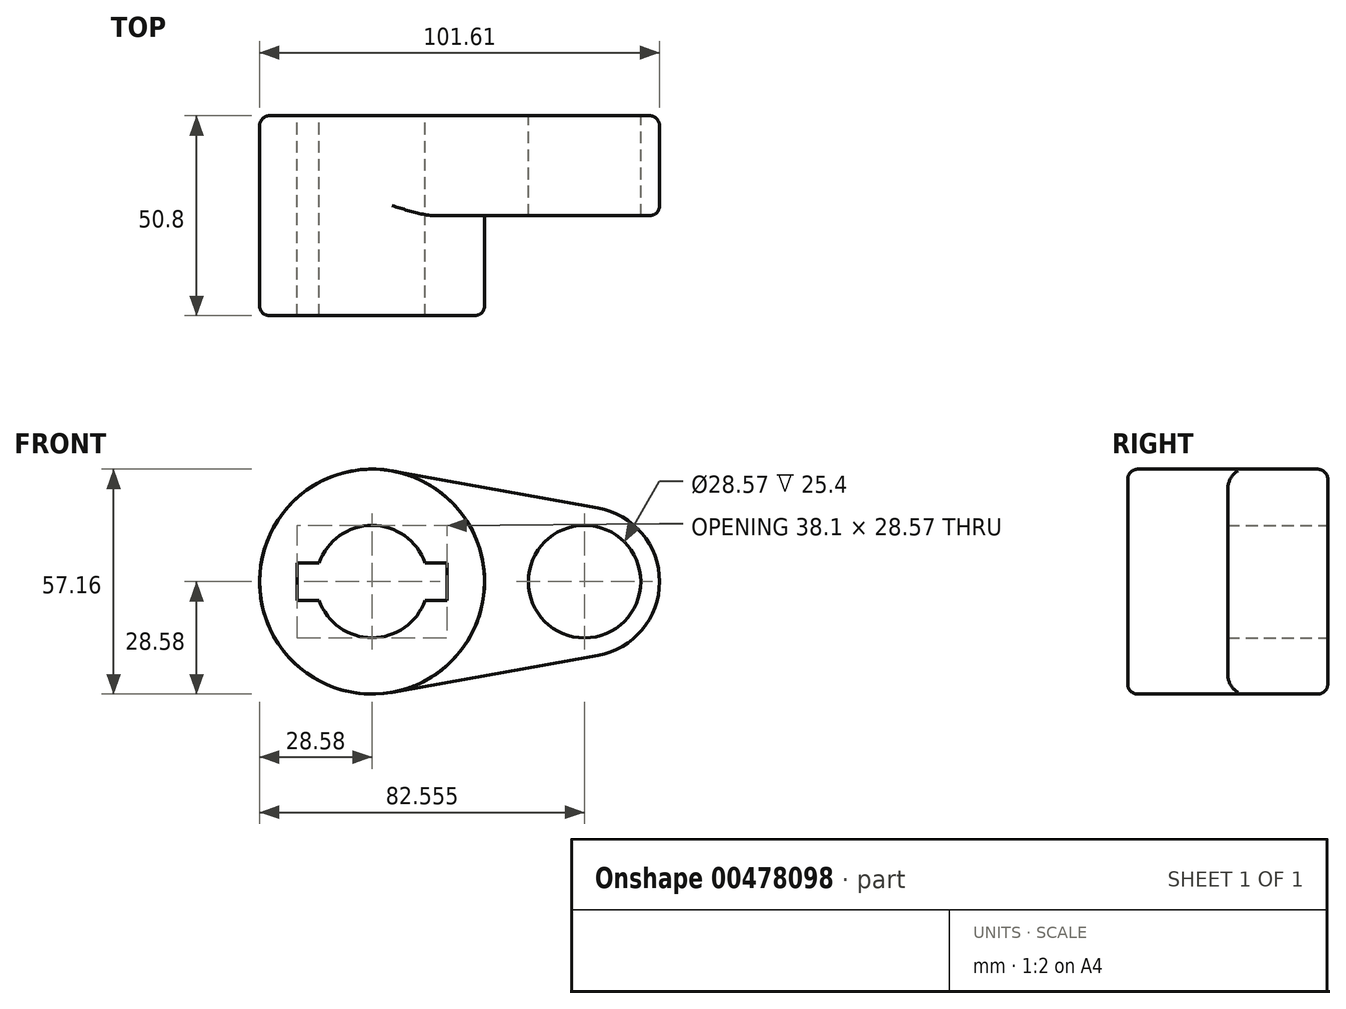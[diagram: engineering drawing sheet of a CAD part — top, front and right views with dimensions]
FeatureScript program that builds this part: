
annotation { "Feature Type Name" : "Feature", "Feature Type Description" : "" }
export const myFeature = defineFeature(function(context is Context, id is Id, definition is map)
    precondition{}
    {
        {
            var Q0;
            Q0=qCreatedBy(makeId("Front.planeOp"),FACE);
            var sketch = newSketch(context, id + "F0", { "sketchPlane" : qUnion([Q0])});
            skCircle(sketch, "E0", {"center": v(0, 0) * mm, "radius": 28.58 * mm});
            skCircle(sketch, "E1", {"center": v(53.98, 0) * mm, "radius": 19.05 * mm});
            skLineSegment(sketch, "E2", {"start": v(5.04, 28.13) * mm, "end": v(57.34, 18.75) * mm});
            skLineSegment(sketch, "E3", {"start": v(5.04, -28.13) * mm, "end": v(57.34, -18.75) * mm});
            skCircle(sketch, "E4", {"center": v(0, 0) * mm, "radius": 14.29 * mm});
            skCircle(sketch, "E5", {"center": v(53.98, 0) * mm, "radius": 14.29 * mm});
            skLineSegment(sketch, "E6.bottom", {"start": v(19.05, -4.76) * mm, "end": v(-19.05, -4.76) * mm});
            skLineSegment(sketch, "E6.top", {"start": v(19.05, 4.76) * mm, "end": v(-19.05, 4.76) * mm});
            skLineSegment(sketch, "E6.left", {"start": v(19.05, -4.76) * mm, "end": v(19.05, 4.76) * mm});
            skLineSegment(sketch, "E6.right", {"start": v(-19.05, -4.76) * mm, "end": v(-19.05, 4.76) * mm});
            skSolve(sketch);
        }
        {
            var Q0;
            {var subQ0=sQuery(id+"F0.wireOp",EDGE,"E2");Q0=makeQuery(id+"F0.imprint","IMPRINT",FACE,{"disambiguationData":[TD([[makeQuery(id+"F0.imprint","IMPRINT",EDGE,{"derivedFrom":subQ0}),-1.0]])]});}
            var Q1;
            {var subQ7=sQuery(id+"F0.wireOp",EDGE,"E6.left");Q1=makeQuery(id+"F0.imprint","IMPRINT",FACE,{"disambiguationData":[TD([[makeQuery(id+"F0.imprint","IMPRINT",EDGE,{"derivedFrom":subQ7}),-1.0]])]});}
            var Q2;
            Q2=makeQuery(id+"F0.imprint","IMPRINT",FACE,{"disambiguationData":[TD([[makeQuery(id+"F0.imprint","IMPRINT",EDGE,{"derivedFrom":sQuery(id+"F0.wireOp",EDGE,"E5")}),-1.0]])]});
            extrude(context, id + "F1", {"entities" : qUnion([Q0, Q1, Q2]), "depth" : 25.4 * mm});
        }
        {
            var Q0;
            {var subQ7=sQuery(id+"F0.wireOp",EDGE,"E6.left");Q0=makeQuery(id+"F0.imprint","IMPRINT",FACE,{"disambiguationData":[TD([[makeQuery(id+"F0.imprint","IMPRINT",EDGE,{"derivedFrom":subQ7}),-1.0]])]});}
            extrude(context, id + "F2", {"entities" : qUnion([Q0]), "operationType" : NewBodyOperationType.ADD, "depth" : 50.8 * mm});
        }
        {
            var Q0;
            Q0=makeQuery(id+"F2.opExtrude","CAP_EDGE",EDGE,{"disambiguationData":[OSD([sQuery(id+"F0.wireOp",EDGE,"E0")])],"isStart":false});
            fillet(context, id + "F3", {"entities" : qUnion([Q0]), "radius" : 2.54 * mm, "tangentPropagation" : true, "allowEdgeOverflow" : false});
        }
        {
            var Q0;
            Q0=makeQuery(id+"F1.opExtrude","CAP_EDGE",EDGE,{"disambiguationData":[OSD([sQuery(id+"F0.wireOp",EDGE,"E1")])],"isStart":false});
            fillet(context, id + "F4", {"entities" : qUnion([Q0]), "radius" : 2.54 * mm, "tangentPropagation" : true, "allowEdgeOverflow" : false});
        }
        {
            var Q0;
            Q0=makeQuery(id+"F1.opExtrude","CAP_EDGE",EDGE,{"disambiguationData":[OSD([sQuery(id+"F0.wireOp",EDGE,"E3")])],"isStart":true});
            fillet(context, id + "F5", {"entities" : qUnion([Q0]), "radius" : 2.54 * mm, "tangentPropagation" : true, "allowEdgeOverflow" : false});
        }
    });
